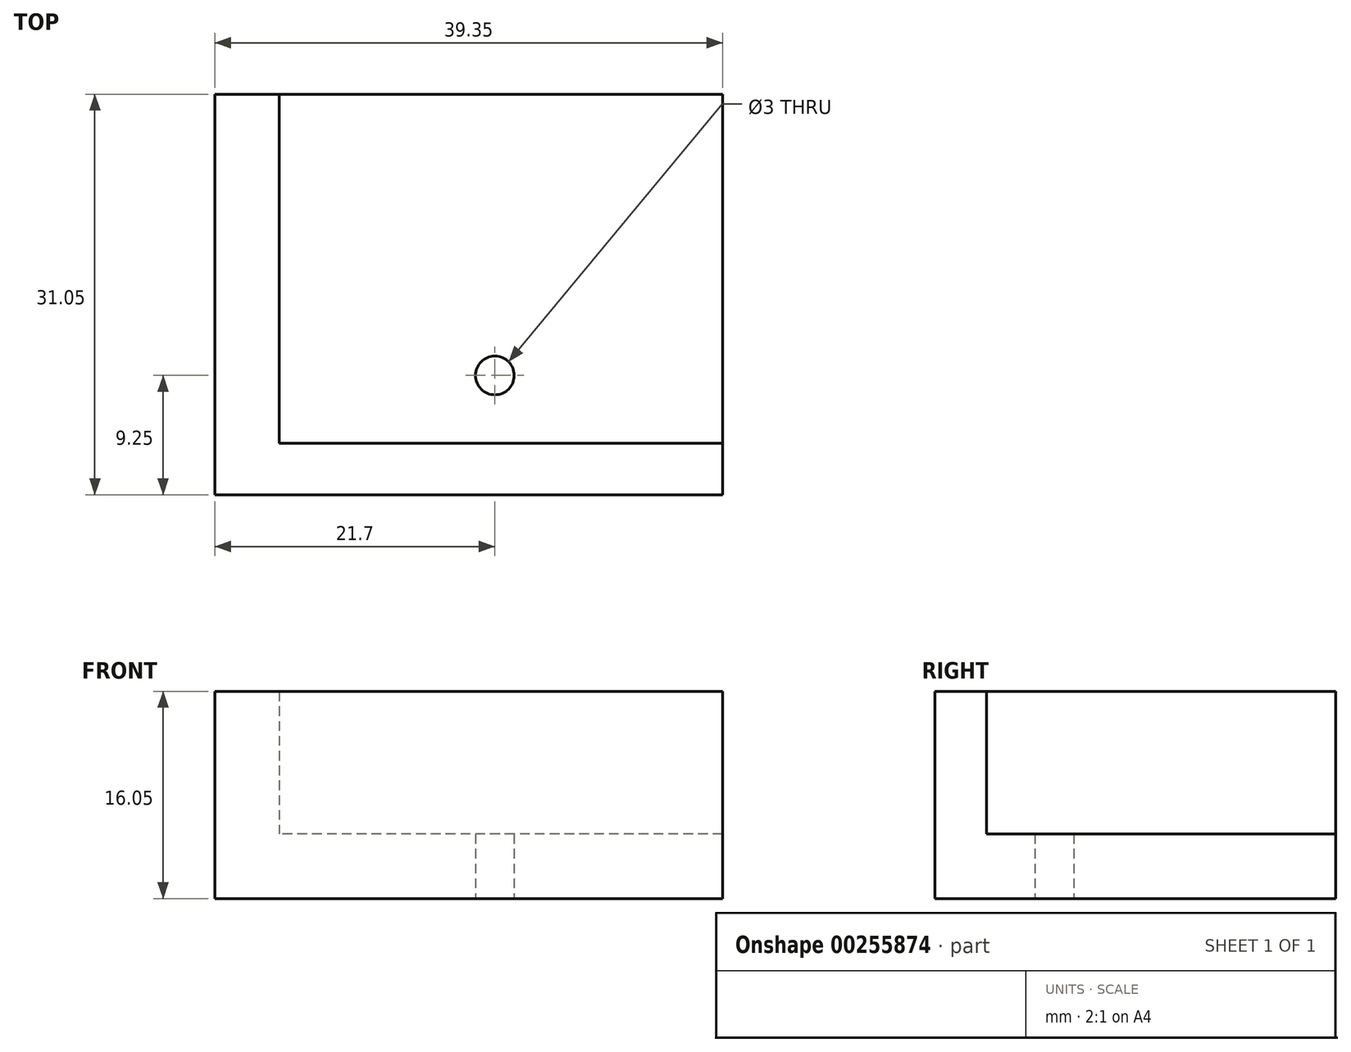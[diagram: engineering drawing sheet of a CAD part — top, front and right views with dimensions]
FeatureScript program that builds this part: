
annotation { "Feature Type Name" : "Feature", "Feature Type Description" : "" }
export const myFeature = defineFeature(function(context is Context, id is Id, definition is map)
    precondition{}
    {
        {
            var Q0;
            Q0=qCreatedBy(makeId("Top.planeOp"),FACE);
            var sketch = newSketch(context, id + "F0", { "sketchPlane" : qUnion([Q0])});
            skCircle(sketch, "E0", {"center": v(0, 0) * mm, "radius": 2.5 * mm, "construction": true});
            skLineSegment(sketch, "E1.bottom", {"start": v(10, 20) * mm, "end": v(-15.35, 20) * mm});
            skLineSegment(sketch, "E1.top", {"start": v(10, -11.05) * mm, "end": v(-15.35, -11.05) * mm});
            skLineSegment(sketch, "E1.left", {"start": v(10, 20) * mm, "end": v(10, -11.05) * mm});
            skLineSegment(sketch, "E1.right", {"start": v(-15.35, 20) * mm, "end": v(-15.35, -11.05) * mm});
            skLineSegment(sketch, "E2", {"start": v(-7.05, 20) * mm, "end": v(-7.05, -7.05) * mm, "construction": true});
            skLineSegment(sketch, "E3", {"start": v(-7.05, -7.05) * mm, "end": v(10, -7.05) * mm, "construction": true});
            skCircle(sketch, "E4", {"center": v(6.35, -1.8) * mm, "radius": 1.5 * mm});
            skSolve(sketch);
        }
        {
            var Q0;
            Q0 = qSketchRegion(id + "F0", true);
            extrude(context, id + "F1", {"entities" : qUnion([Q0]), "depth" : 5 * mm});
        }
        {
            var Q0;
            Q0=makeQuery(id+"F1.opExtrude","CAP_FACE",FACE,{"disambiguationData":[OSD([sQuery(id+"F0.wireOp",EDGE,"E0"),sQuery(id+"F0.wireOp",EDGE,"E1.bottom"),sQuery(id+"F0.wireOp",EDGE,"E1.top"),sQuery(id+"F0.wireOp",EDGE,"E1.left"),sQuery(id+"F0.wireOp",EDGE,"E1.right")])],"isStart":false});
            var sketch = newSketch(context, id + "F2", { "sketchPlane" : qUnion([Q0])});
            skLineSegment(sketch, "E5", {"start": v(-15.35, 20) * mm, "end": v(-15.35, -11.05) * mm});
            skLineSegment(sketch, "E6", {"start": v(-15.35, -11.05) * mm, "end": v(10, -11.05) * mm});
            skLineSegment(sketch, "E7", {"start": v(10, -11.05) * mm, "end": v(10, -7.05) * mm});
            skLineSegment(sketch, "E8", {"start": v(10, -7.05) * mm, "end": v(-10.35, -7.05) * mm});
            skLineSegment(sketch, "E9", {"start": v(-10.35, -7.05) * mm, "end": v(-10.35, 20) * mm});
            skLineSegment(sketch, "E10", {"start": v(-10.35, 20) * mm, "end": v(-15.35, 20) * mm});
            skSolve(sketch);
        }
        {
            var Q0;
            Q0 = qSketchRegion(id + "F2", true);
            extrude(context, id + "F3", {"entities" : qUnion([Q0]), "operationType" : NewBodyOperationType.ADD, "depth" : 8.55 * mm + 2.5 * mm});
        }
        {
            var Q0;
            Q0=makeQuery(id+"F3.boolean.opBoolean","MERGE",FACE,{"derivedFrom":[makeQuery(id+"F1.opExtrude","SWEPT_FACE",FACE,{"disambiguationData":[OSD([sQuery(id+"F0.wireOp",EDGE,"E1.left")])]}),makeQuery(id+"F3.opExtrude","SWEPT_FACE",FACE,{"disambiguationData":[OSD([sQuery(id+"F2.wireOp",EDGE,"E7")])]})]});
            var sketch = newSketch(context, id + "F4", { "sketchPlane" : qUnion([Q0])});
            skLineSegment(sketch, "E11", {"start": v(-11.05, 16.05) * mm, "end": v(-7.05, 16.05) * mm});
            skLineSegment(sketch, "E12", {"start": v(-7.05, 16.05) * mm, "end": v(-7.05, 5) * mm});
            skLineSegment(sketch, "E13", {"start": v(-7.05, 5) * mm, "end": v(20, 5) * mm});
            skLineSegment(sketch, "E14", {"start": v(20, 5) * mm, "end": v(20, 0) * mm});
            skLineSegment(sketch, "E15", {"start": v(20, 0) * mm, "end": v(-11.05, 0) * mm});
            skLineSegment(sketch, "E16", {"start": v(-11.05, 0) * mm, "end": v(-11.05, 16.05) * mm});
            skSolve(sketch);
        }
        {
            var Q0;
            Q0 = qSketchRegion(id + "F4", true);
            extrude(context, id + "F5", {"entities" : qUnion([Q0]), "operationType" : NewBodyOperationType.ADD, "depth" : 14 * mm});
        }
    });
